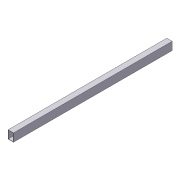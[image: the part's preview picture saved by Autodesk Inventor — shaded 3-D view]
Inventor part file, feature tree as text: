
AUTODESK INVENTOR PART (.ipt)
format: ipt  version: 2012 (Build 160160000, 160)  size: 73,728 bytes
history: native  units: in
note: dims shown in document units (in); Inventor stores cm internally (conversion verified against a paired STEP export)
features: extrude x1, sketch x1
ambient origin geometry x8: Origin, YZ Plane, XZ Plane, XY Plane, X Axis, Y Axis, Z Axis, Center Point
bodies: Solid1 (feature_tree)
feature tree (2):
  extrude  "Extrusion1"  Depth=0.125in
  sketch  "Sketch1"  dims[d4=59.0in d5=0.0in d13=0.125in d14=2.0in d15=3.0in d16=0.125in d17=0.125in d18=0.125in]
